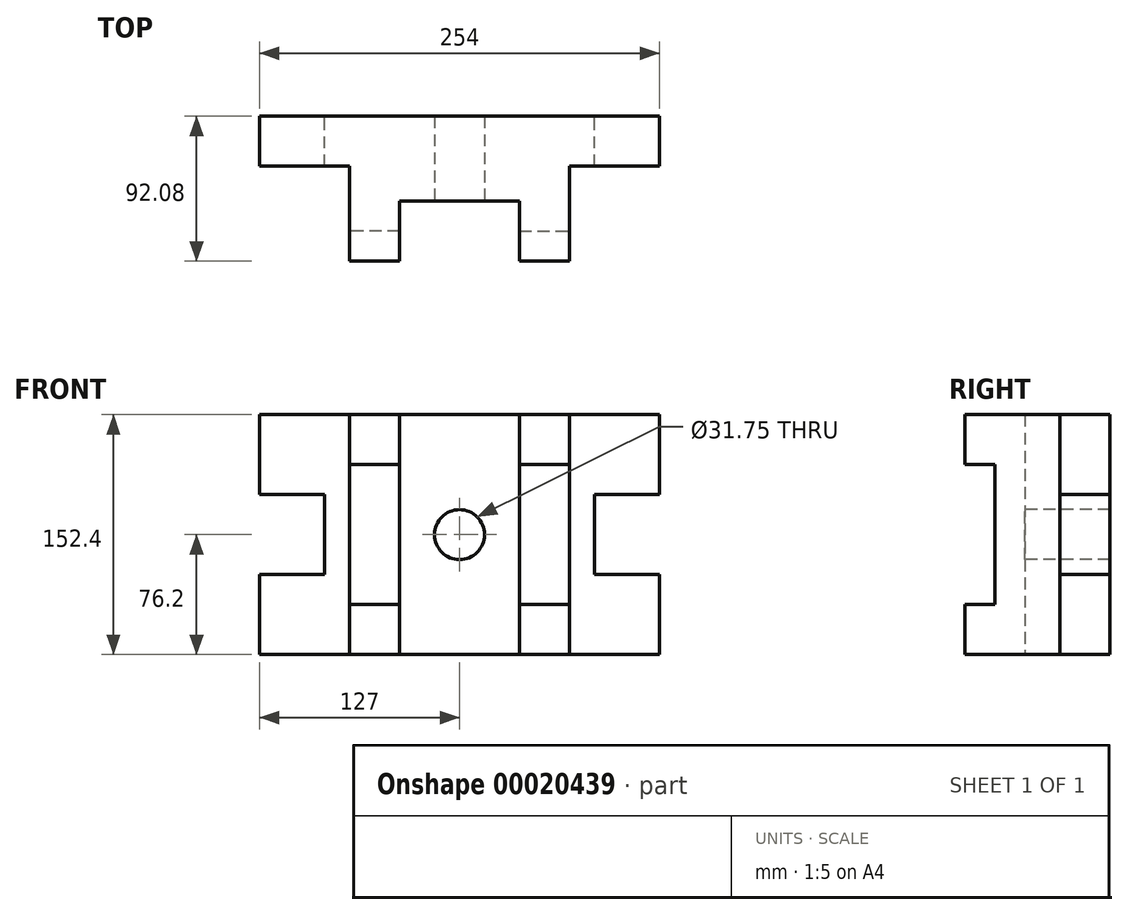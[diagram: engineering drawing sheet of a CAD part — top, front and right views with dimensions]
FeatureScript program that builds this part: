
annotation { "Feature Type Name" : "Feature", "Feature Type Description" : "" }
export const myFeature = defineFeature(function(context is Context, id is Id, definition is map)
    precondition{}
    {
        {
            var Q0;
            Q0=qCreatedBy(makeId("Front.planeOp"),FACE);
            var sketch = newSketch(context, id + "F0", { "sketchPlane" : qUnion([Q0])});
            skLineSegment(sketch, "E0.rect.bottom", {"start": v(127, 76.2) * mm, "end": v(0, 76.2) * mm});
            skLineSegment(sketch, "E0.rect.top", {"start": v(127, -76.2) * mm, "end": v(0, -76.2) * mm});
            skLineSegment(sketch, "E0.rect.left", {"start": v(127, 76.2) * mm, "end": v(127, 25.4) * mm});
            skPoint(sketch, "E0.rect.middle", {"position": v(0, 0) * mm});
            skLineSegment(sketch, "E1.bottom", {"start": v(127, -25.4) * mm, "end": v(85.72, -25.4) * mm});
            skLineSegment(sketch, "E1.top", {"start": v(127, 25.4) * mm, "end": v(85.72, 25.4) * mm});
            skLineSegment(sketch, "E1.right", {"start": v(85.72, -25.4) * mm, "end": v(85.72, 25.4) * mm});
            skLineSegment(sketch, "E2", {"start": v(0, 76.2) * mm, "end": v(0, -76.2) * mm});
            skLineSegment(sketch, "E3.trimOffspring", {"start": v(127, -25.4) * mm, "end": v(127, -76.2) * mm});
            skLineSegment(sketch, "E4", {"start": v(69.85, 76.2) * mm, "end": v(69.85, -76.2) * mm});
            skSolve(sketch);
        }
        {
            var Q0;
            {var subQ1=sQuery(id+"F0.wireOp",EDGE,"E2");Q0=makeQuery(id+"F0.imprint","IMPRINT",FACE,{"disambiguationData":[TD([[makeQuery(id+"F0.imprint","IMPRINT",EDGE,{"derivedFrom":subQ1}),1.0]])]});}
            extrude(context, id + "F1", {"entities" : qUnion([Q0]), "depth" : 92.07 * mm});
        }
        {
            var Q0;
            {var subQ2=sQuery(id+"F0.wireOp",EDGE,"E0.rect.left");Q0=makeQuery(id+"F0.imprint","IMPRINT",FACE,{"disambiguationData":[TD([[makeQuery(id+"F0.imprint","IMPRINT",EDGE,{"derivedFrom":subQ2}),-1.0]])]});}
            extrude(context, id + "F2", {"entities" : qUnion([Q0]), "operationType" : NewBodyOperationType.ADD, "depth" : 31.75 * mm});
        }
        {
            var Q0;
            Q0=makeQuery(id+"F1.opExtrude","CAP_FACE",FACE,{"disambiguationData":[OSD([sQuery(id+"F0.wireOp",EDGE,"E0.rect.bottom"),sQuery(id+"F0.wireOp",EDGE,"E0.rect.top"),sQuery(id+"F0.wireOp",EDGE,"E2"),sQuery(id+"F0.wireOp",EDGE,"E4")])],"isStart":false});
            var sketch = newSketch(context, id + "F3", { "sketchPlane" : qUnion([Q0])});
            skLineSegment(sketch, "E5.bottom", {"start": v(0, 76.2) * mm, "end": v(38.1, 76.2) * mm});
            skLineSegment(sketch, "E5.top", {"start": v(0, -76.2) * mm, "end": v(38.1, -76.2) * mm});
            skLineSegment(sketch, "E5.left", {"start": v(0, 76.2) * mm, "end": v(0, -76.2) * mm});
            skLineSegment(sketch, "E5.right", {"start": v(38.1, 76.2) * mm, "end": v(38.1, -76.2) * mm});
            skSolve(sketch);
        }
        {
            var Q0;
            Q0=makeQuery(id+"F3.imprint","IMPRINT",FACE,{"disambiguationData":[TD([[makeQuery(id+"F3.imprint","IMPRINT",EDGE,{"derivedFrom":sQuery(id+"F3.wireOp",EDGE,"E5.bottom")}),1.0]])]});
            extrude(context, id + "F4", {"entities" : qUnion([Q0]), "operationType" : NewBodyOperationType.REMOVE, "oppositeDirection" : true, "depth" : 38.1 * mm});
        }
        {
            var Q0;
            Q0=makeQuery(id+"F1.opExtrude","CAP_FACE",FACE,{"disambiguationData":[OSD([sQuery(id+"F0.wireOp",EDGE,"E0.rect.bottom"),sQuery(id+"F0.wireOp",EDGE,"E0.rect.top"),sQuery(id+"F0.wireOp",EDGE,"E2"),sQuery(id+"F0.wireOp",EDGE,"E4")])],"isStart":false});
            var sketch = newSketch(context, id + "F5", { "sketchPlane" : qUnion([Q0])});
            skLineSegment(sketch, "E6.bottom", {"start": v(38.1, 76.2) * mm, "end": v(69.85, 76.2) * mm});
            skLineSegment(sketch, "E6.top", {"start": v(38.1, 44.45) * mm, "end": v(69.85, 44.45) * mm});
            skLineSegment(sketch, "E6.left", {"start": v(38.1, 76.2) * mm, "end": v(38.1, 44.45) * mm});
            skLineSegment(sketch, "E6.right", {"start": v(69.85, 76.2) * mm, "end": v(69.85, 44.45) * mm});
            skLineSegment(sketch, "E7.bottom", {"start": v(69.85, -76.2) * mm, "end": v(38.1, -76.2) * mm});
            skLineSegment(sketch, "E7.top", {"start": v(69.85, -44.45) * mm, "end": v(38.1, -44.45) * mm});
            skLineSegment(sketch, "E7.left", {"start": v(69.85, -76.2) * mm, "end": v(69.85, -44.45) * mm});
            skLineSegment(sketch, "E7.right", {"start": v(38.1, -76.2) * mm, "end": v(38.1, -44.45) * mm});
            skSolve(sketch);
        }
        {
            var Q0;
            {var subQ2=sQuery(id+"F5.wireOp",EDGE,"E6.top");Q0=makeQuery(id+"F5.imprint","IMPRINT",FACE,{"disambiguationData":[TD([[makeQuery(id+"F5.imprint","IMPRINT",EDGE,{"derivedFrom":subQ2}),-1.0]])]});}
            extrude(context, id + "F6", {"entities" : qUnion([Q0]), "operationType" : NewBodyOperationType.REMOVE, "oppositeDirection" : true, "depth" : 19.05 * mm});
        }
        {
            var Q0;
            Q0=makeQuery(id+"F1.opExtrude","SWEPT_BODY",BODY,{"disambiguationData":[OSD([sQuery(id+"F0.wireOp",EDGE,"E0.rect.bottom"),sQuery(id+"F0.wireOp",EDGE,"E0.rect.top"),sQuery(id+"F0.wireOp",EDGE,"E2"),sQuery(id+"F0.wireOp",EDGE,"E4")])]});
            var Q1;
            Q1=makeQuery(id+"F1.opExtrude","SWEPT_FACE",FACE,{"disambiguationData":[OSD([sQuery(id+"F0.wireOp",EDGE,"E2")])]});
            mirror(context, id + "F7", {"operationType" : NewBodyOperationType.ADD, "entities" : qUnion([Q0]), "mirrorPlane" : qUnion([Q1])});
        }
        {
            var Q0;
            {var subQ0=makeQuery(id+"F4.boolean.opBoolean","COPY",FACE,{"derivedFrom":makeQuery(id+"F4.opExtrude","CAP_FACE",FACE,{"disambiguationData":[OSD([sQuery(id+"F3.wireOp",EDGE,"E5.bottom"),sQuery(id+"F3.wireOp",EDGE,"E5.top"),sQuery(id+"F3.wireOp",EDGE,"E5.left"),sQuery(id+"F3.wireOp",EDGE,"E5.right")])],"isStart":false})});Q0=makeQuery(id+"F7.boolean.opBoolean","MERGE",FACE,{"derivedFrom":[subQ0,makeQuery(id+"F7.opPattern","COPY",FACE,{"derivedFrom":subQ0,"instanceName":"1"})]});}
            var sketch = newSketch(context, id + "F8", { "sketchPlane" : qUnion([Q0])});
            skCircle(sketch, "E8", {"center": v(0, 0) * mm, "radius": 15.88 * mm});
            skSolve(sketch);
        }
        {
            var Q0;
            Q0=makeQuery(id+"F8.imprint","IMPRINT",FACE,{"disambiguationData":[TD([[makeQuery(id+"F8.imprint","IMPRINT",EDGE,{"derivedFrom":sQuery(id+"F8.wireOp",EDGE,"E8")}),1.0]])]});
            extrude(context, id + "F9", {"entities" : qUnion([Q0]), "operationType" : NewBodyOperationType.REMOVE, "oppositeDirection" : true, "depth" : 90.98 * mm});
        }
    });
